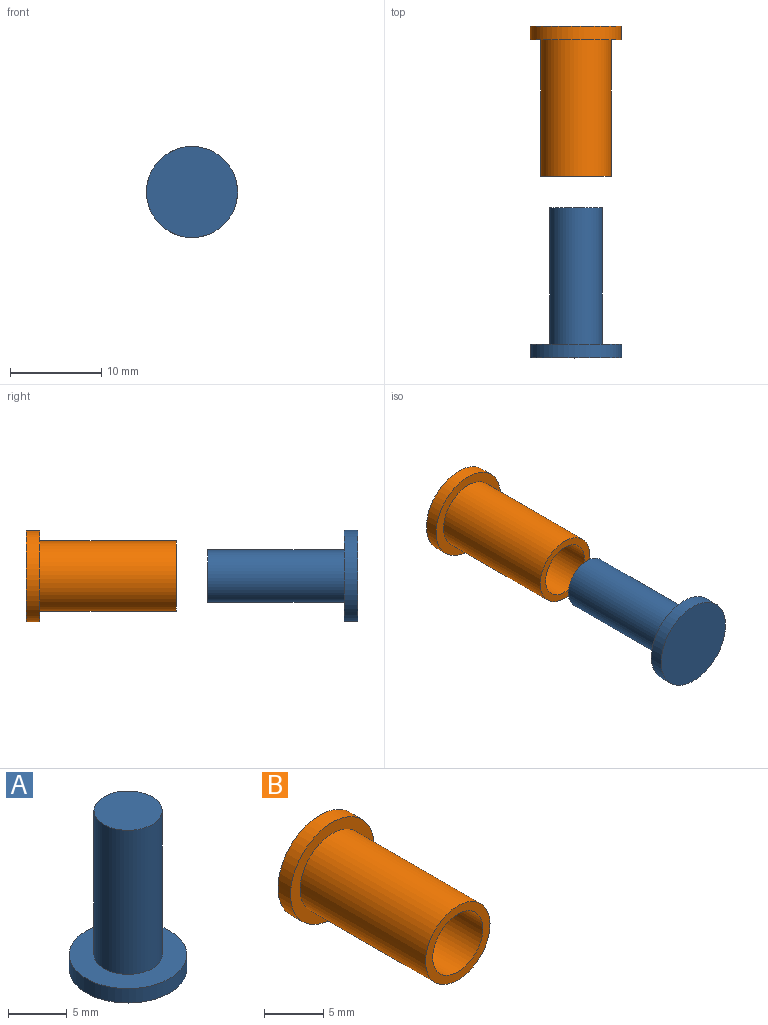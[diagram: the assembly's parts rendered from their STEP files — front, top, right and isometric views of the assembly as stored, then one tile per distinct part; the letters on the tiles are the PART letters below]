
ASSEMBLY  parts=2 mates=1
PART A: 5 faces, bbox 10x10x16.5 mm
  f0: cylinder r=5mm len=10mm, axis (0,0,-1), area 47.1mm2, adj f1,f2
  f1: plane 10x10mm, normal (0,0,1), area 52.1mm2, adj f0,f3
  f2: plane 10x10mm, normal (0,0,-1), area 78.5mm2, adj f0
  f3: cylinder r=2.9mm len=15mm, axis (0,0,-1), area 273.3mm2, adj f1,f4
  f4: plane 5.8x5.8mm, normal (0,0,1), area 26.4mm2, adj f3
PART B: 7 faces, bbox 10x16.5x10 mm
  f0: cylinder r=5mm len=10mm, axis (0,1,0), area 47.1mm2, adj f1,f2
  f1: plane 10x10mm, normal (0,-1,0), area 32mm2, adj f0,f3
  f2: plane 10x10mm, normal (0,1,0), area 78.5mm2, adj f0
  f3: cylinder r=3.85mm len=15mm, axis (0,1,0), area 362.9mm2, adj f1,f4
  f4: plane 7.7x7.7mm, normal (0,-1,0), area 18.3mm2, adj f3,f5
  f5: cylinder r=3mm len=15mm, axis (0,-1,0), area 282.7mm2, adj f4,f6
  f6: plane 6x6mm, normal (0,-1,0), area 28.3mm2, adj f5
PLACE A rot(axis=(-1,0,0),90deg) t=(6.2,-35.62,3.69)mm
PLACE B rot(axis=(0,-1,0),0deg) t=(6.2,0.79,3.69)mm fixed
MATE slider A.f3 <-> B.f5  axis (0,1,0) through (6.2,-19.12,3.69)mm
